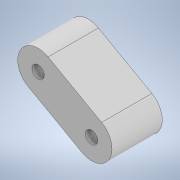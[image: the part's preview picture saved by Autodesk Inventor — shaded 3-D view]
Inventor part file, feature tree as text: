
AUTODESK INVENTOR PART (.ipt)
format: ipt  version: 2020 (Build 240168000, 168)  size: 179,712 bytes
history: native  units: mm
features: other x3, sketch x1, plane x1, extrude x1, thicken_offset x1, reference x1
ambient origin geometry x8: Origin, YZ Plane, XZ Plane, XY Plane, X Axis, Y Axis, Z Axis, Center Point
bodies: Solid1 (feature_tree)
feature tree (8):
  sketch  "Sketch1"  dims[d0=8.0mm d1=3.0mm d2=3.0mm d3=10.0mm d4=0.0mm d5=1.0mm d6=1.0mm]
  plane  "Work Plane1"
  extrude  "Extrusion1"  Depth=10.0mm
  thicken_offset  "Thicken1"
  reference  "Reference1"
  parser-record x1  (decoder bookkeeping rows leaked as tree rows — omitted from the tree; the rows remain in map.json)
  other  "reducer_3.iam"
  other  "motor_h_4:1"
note: 1 file-system path scrubbed to <path> (originals preserved in map.json)
